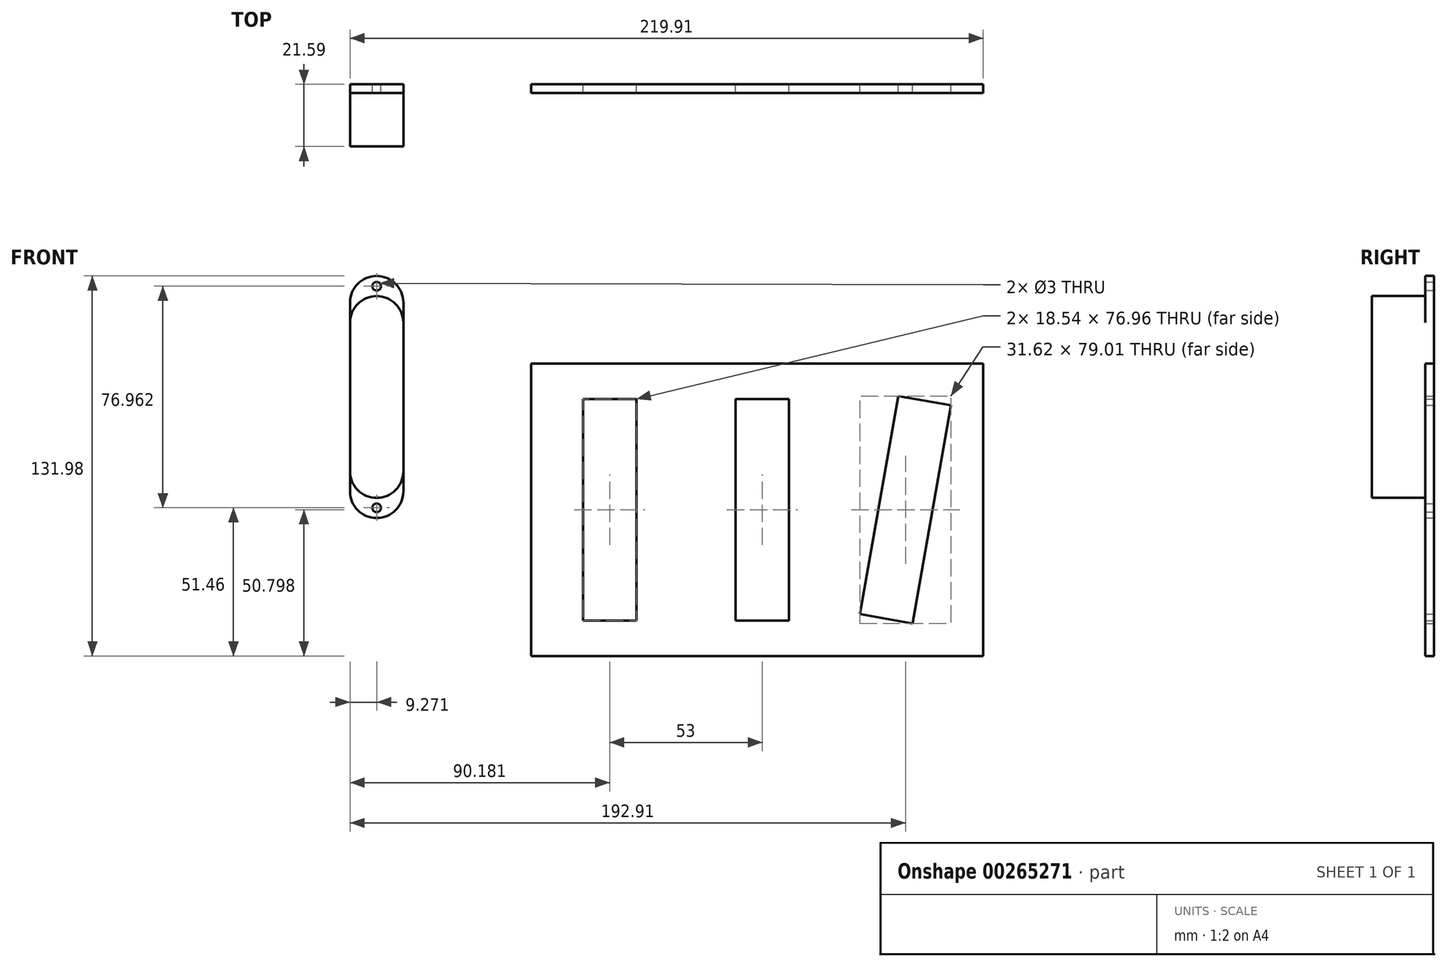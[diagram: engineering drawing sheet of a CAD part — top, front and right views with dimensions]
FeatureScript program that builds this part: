
annotation { "Feature Type Name" : "Feature", "Feature Type Description" : "" }
export const myFeature = defineFeature(function(context is Context, id is Id, definition is map)
    precondition{}
    {
        {
            var Q0;
            Q0=qCreatedBy(makeId("Front.planeOp"),FACE);
            var sketch = newSketch(context, id + "F0", { "sketchPlane" : qUnion([Q0])});
            skLineSegment(sketch, "E0", {"start": v(-108.75, 25.78) * mm, "end": v(-4.88, 25.78) * mm, "construction": true});
            skLineSegment(sketch, "E1", {"start": v(-52.94, 79.68) * mm, "end": v(-52.94, -28.12) * mm, "construction": true});
            skPoint(sketch, "E2", {"position": v(-52.94, 25.78) * mm});
            skCircle(sketch, "E3", {"center": v(-52.94, 64.26) * mm, "radius": 1.5 * mm});
            skCircle(sketch, "E4", {"center": v(-52.94, -12.7) * mm, "radius": 1.5 * mm});
            skPoint(sketch, "E5", {"position": v(-62.21, 51.56) * mm});
            skPoint(sketch, "E6", {"position": v(-43.67, 51.56) * mm});
            skLineSegment(sketch, "E7", {"start": v(-62.21, 51.56) * mm, "end": v(-43.67, 51.56) * mm, "construction": true});
            skArc(sketch, "E8", {"start": v(-43.67, 51.56) * mm, "mid": v(-52.94, 60.83) * mm, "end": v(-62.21, 51.56) * mm});
            skLineSegment(sketch, "E9", {"start": v(-62.21, 0) * mm, "end": v(-43.67, 0) * mm, "construction": true});
            skArc(sketch, "E10", {"start": v(-62.21, 0) * mm, "mid": v(-52.94, -9.27) * mm, "end": v(-43.67, 0) * mm});
            skLineSegment(sketch, "E11", {"start": v(-62.21, 51.56) * mm, "end": v(-62.21, 0) * mm});
            skLineSegment(sketch, "E12", {"start": v(-43.67, 51.56) * mm, "end": v(-43.67, 0) * mm});
            skArc(sketch, "E13", {"start": v(-43.67, 58.55) * mm, "mid": v(-52.94, 67.82) * mm, "end": v(-62.21, 58.55) * mm});
            skLineSegment(sketch, "E14", {"start": v(-62.21, 58.55) * mm, "end": v(-43.67, 58.55) * mm, "construction": true});
            skLineSegment(sketch, "E15", {"start": v(-62.21, 58.55) * mm, "end": v(-62.21, 51.56) * mm});
            skLineSegment(sketch, "E16", {"start": v(-43.67, 58.55) * mm, "end": v(-43.67, 51.56) * mm});
            skArc(sketch, "E17", {"start": v(-62.21, -6.98) * mm, "mid": v(-52.94, -16.26) * mm, "end": v(-43.67, -6.98) * mm});
            skLineSegment(sketch, "E18", {"start": v(-62.21, -6.98) * mm, "end": v(-43.67, -6.98) * mm, "construction": true});
            skLineSegment(sketch, "E19", {"start": v(-62.21, -6.98) * mm, "end": v(-62.21, 0) * mm});
            skLineSegment(sketch, "E20", {"start": v(-43.67, -6.98) * mm, "end": v(-43.67, 0) * mm});
            skPoint(sketch, "E21", {"position": v(-52.94, 60.83) * mm});
            skPoint(sketch, "E22", {"position": v(-52.94, 67.82) * mm});
            skPoint(sketch, "E23", {"position": v(-52.94, -9.27) * mm});
            skPoint(sketch, "E24", {"position": v(-52.94, -16.26) * mm});
            skSolve(sketch);
        }
        {
            var Q0;
            Q0=qCreatedBy(makeId("Front.planeOp"),FACE);
            var sketch = newSketch(context, id + "F1", { "sketchPlane" : qUnion([Q0])});
            skLineSegment(sketch, "E25.bottom", {"start": v(0.7, 37.44) * mm, "end": v(157.7, 37.44) * mm});
            skLineSegment(sketch, "E25.top", {"start": v(0.7, -64.16) * mm, "end": v(157.7, -64.16) * mm});
            skLineSegment(sketch, "E25.left", {"start": v(0.7, 37.44) * mm, "end": v(0.7, -64.16) * mm});
            skLineSegment(sketch, "E25.right", {"start": v(157.7, 37.44) * mm, "end": v(157.7, -64.16) * mm});
            skPoint(sketch, "E25.middle", {"position": v(79.2, -13.36) * mm});
            skLineSegment(sketch, "E26", {"start": v(0.7, -13.36) * mm, "end": v(157.7, -13.36) * mm, "construction": true});
            skLineSegment(sketch, "E27", {"start": v(18.7, 25.12) * mm, "end": v(18.7, -51.84) * mm});
            skLineSegment(sketch, "E28", {"start": v(71.7, 25.12) * mm, "end": v(71.7, -51.84) * mm});
            skLineSegment(sketch, "E29", {"start": v(128.25, 26.14) * mm, "end": v(114.89, -49.65) * mm});
            skLineSegment(sketch, "E30", {"start": v(18.7, 25.12) * mm, "end": v(37.24, 25.12) * mm});
            skLineSegment(sketch, "E31", {"start": v(37.24, 25.12) * mm, "end": v(37.24, -51.84) * mm});
            skLineSegment(sketch, "E32", {"start": v(37.24, -51.84) * mm, "end": v(18.7, -51.84) * mm});
            skLineSegment(sketch, "E33", {"start": v(71.7, 25.12) * mm, "end": v(90.24, 25.12) * mm});
            skLineSegment(sketch, "E34", {"start": v(90.24, 25.12) * mm, "end": v(90.24, -51.84) * mm});
            skLineSegment(sketch, "E35", {"start": v(90.24, -51.84) * mm, "end": v(71.7, -51.84) * mm});
            skLineSegment(sketch, "E36", {"start": v(128.25, 26.14) * mm, "end": v(146.51, 22.92) * mm});
            skLineSegment(sketch, "E37", {"start": v(146.51, 22.92) * mm, "end": v(133.15, -52.87) * mm});
            skLineSegment(sketch, "E38", {"start": v(133.15, -52.87) * mm, "end": v(114.89, -49.65) * mm});
            skLineSegment(sketch, "E39", {"start": v(137.38, 24.53) * mm, "end": v(124.02, -51.26) * mm});
            skPoint(sketch, "E40", {"position": v(130.7, -13.36) * mm});
            skSolve(sketch);
        }
        {
            var Q0;
            Q0=makeQuery(id+"F0.imprint","IMPRINT",FACE,{"disambiguationData":[TD([[makeQuery(id+"F0.imprint","IMPRINT",EDGE,{"derivedFrom":sQuery(id+"F0.wireOp",EDGE,"E8")}),1.0]])]});
            extrude(context, id + "F2", {"entities" : qUnion([Q0]), "depth" : 21.59 * mm});
        }
        {
            var Q0;
            Q0 = qSketchRegion(id + "F0", true);
            extrude(context, id + "F3", {"entities" : qUnion([Q0]), "operationType" : NewBodyOperationType.ADD, "depth" : 3 * mm});
        }
        {
            var Q0;
            Q0=makeQuery(id+"F1.imprint","IMPRINT",FACE,{"disambiguationData":[TD([[makeQuery(id+"F1.imprint","IMPRINT",EDGE,{"derivedFrom":sQuery(id+"F1.wireOp",EDGE,"E25.bottom")}),-1.0]])]});
            extrude(context, id + "F4", {"entities" : qUnion([Q0]), "depth" : 3 * mm});
        }
    });
